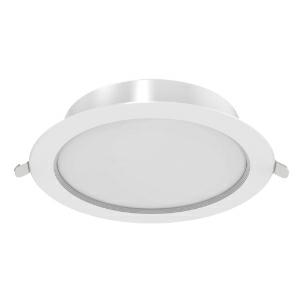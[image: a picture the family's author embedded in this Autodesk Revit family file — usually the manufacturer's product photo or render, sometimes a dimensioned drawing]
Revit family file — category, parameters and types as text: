
# Revit family: leddownlightco-e_rd125-14w-830_540001291100
name_source: partatom
category: Leuchten
revit_build: Autodesk Revit 2016 (Build: 20190508_0715(x64)
units: mm (PartAtom-declared; Revit-internal decimal feet)

## family parameters
Basisbauteil = Fläche
Beim Laden mit Abzugskörper schneiden = Nein
Bemaßung runder Anschluss = Durchmesser verwenden
Gemeinsam genutzt = Nein
Lichtquelle = Nein
Raumberechnungspunkt = Nein
Teiletyp = Normal

## types (1)
- LEDDownlightCo-E Rd125-14W-830 (1 x LED, 1190 lm)
    Approval mark = CE
    Beschreibung = Stylish and compact LED downlight. Sturdy full metal housing. Integrated driver for easier installation. Low height of only 35mm. IP44 on light emitting side.
    CIE Flux Codes = 50 81 96 100 100
    Control Gear = Electronic ballast
    Height = 0 mm  [stored 0 ft]
    Hersteller = OPPLE
    Lamp Light Flux = 1190 lm
    Lamp count = 1
    Lampe = 1 x LED
    Length = 100 mm  [stored 0.328084 ft]
    Luminous efficacy = 85 lm/W
    ModVariant = Nein
    Modell = 540001291100
    Mounting Place = Ceiling
    Mounting Type = Recessed
    Number of Poles = 1
    OnlyDefault = Ja
    Power Factor = 1
    Product Name = LEDDownlightCo-E Rd125-14W-830
    Product group = Downlight Compact
    ProductGroupID = 406
    Protection Class = Protection class II
    Protection Degree = IP 44
    RLX_Detail_Level = 1
    RlxData = <blob elided: 110405 chars, md5=dfffbe18>
    Scheinlast = 14 VA
    Socket = socket
    Standby Power = 0 W
    System Light Flux = 1190 lm
    System Power = 14 W
    Typenbild = 540001291100.jpg
    Typenkommentare = Product without accessories
    URL = http://relux.com
    VarID = ---
    Voltage = 230 V
    Voltage Range = 220-240 V
    Vorgabe-Ansicht = 1800 mm
    Weight = 0.00 kg
    Width = 100 mm  [stored 0.328084 ft]

note: [stored X ft] marks values corroborated as IEEE doubles in the binary element streams (Revit-internal decimal feet)

## geometry (parser evidence)
native form markers: Sweep x9
no freeform markers — native parametric forms only
